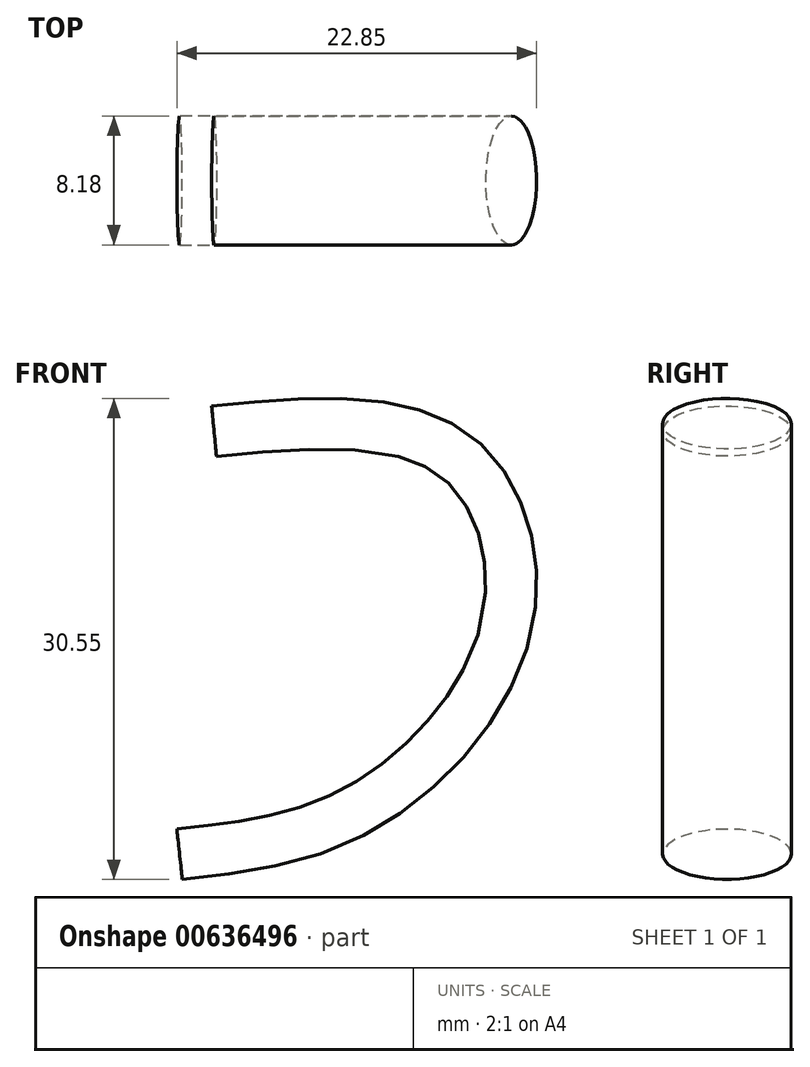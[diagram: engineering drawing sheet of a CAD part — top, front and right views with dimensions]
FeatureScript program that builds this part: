
annotation { "Feature Type Name" : "Feature", "Feature Type Description" : "" }
export const myFeature = defineFeature(function(context is Context, id is Id, definition is map)
    precondition{}
    {
        {
            var Q0;
            Q0=qCreatedBy(makeId("Front.planeOp"),FACE);
            var sketch = newSketch(context, id + "F0", { "sketchPlane" : qUnion([Q0])});
            skLineSegment(sketch, "E0", {"start": v(0, 0) * mm, "end": v(0, 38.86) * mm});
            skSolve(sketch);
        }
        {
            var Q0;
            Q0=qCreatedBy(makeId("Front.planeOp"),FACE);
            var sketch = newSketch(context, id + "F1", { "sketchPlane" : qUnion([Q0])});
            skLineSegment(sketch, "E1", {"start": v(0, 0) * mm, "end": v(11.7, 0) * mm});
            skFitSpline(sketch, "E2", {"points": [v(11.7, 0) * mm, v(19.81, 2.95) * mm, v(26.79, 48.23) * mm], "startDerivative": vector(29.36, 1.38) * mm, "endDerivative": vector(4.15, 84.2) * mm});
            skFitSpline(sketch, "E3", {"points": [v(24.42, 17.48) * mm, v(36.04, 20.46) * mm, v(45.24, 32.13) * mm, v(41.74, 43.02) * mm, v(26.6, 44.43) * mm], "startDerivative": vector(49.86, 5.34) * mm, "endDerivative": vector(-65.27, -6.16) * mm});
            skSolve(sketch);
        }
        {
            var Q0;
            Q0=sQuery(id+"F1.wireOp",EDGE,"E2");
            var Q1;
            Q1=sQuery(id+"F1.wireOp",EDGE,"E1");
            var Q2;
            Q2=sQuery(id+"F0.wireOp",EDGE,"E0");
            revolve(context, id + "F2", {"bodyType" : ToolBodyType.SURFACE, "surfaceEntities" : qUnion([Q0, Q1]), "axis" : qUnion([Q2]), "revolveType" : RevolveType.FULL});
        }
        {
            var Q0;
            Q0=sQuery(id+"F1.wireOp",VERTEX,"E3.end");
            var Q1;
            Q1=sQuery(id+"F1.wireOp",EDGE,"E3");
            cPlane(context, id + "F3", {"entities" : qUnion([Q0, Q1]), "cplaneType" : CPlaneType.CURVE_POINT, "offset" : 25.4 * mm, "width" : 152.4 * mm, "height" : 152.4 * mm});
        }
        {
            var Q0;
            Q0=qCreatedBy(id+"F3.planeOp",FACE);
            var sketch = newSketch(context, id + "F4", { "sketchPlane" : qUnion([Q0])});
            skEllipse(sketch, "E4", {"center": v(0, 41.7) * mm, "majorRadius": 4.09 * mm, "minorRadius": 1.6 * mm, "majorAxis": v(-1, 0)});
            skSolve(sketch);
        }
        {
            var Q0;
            Q0=makeQuery(id+"F4.imprint","IMPRINT",FACE,{"disambiguationData":[TD([[makeQuery(id+"F4.imprint","IMPRINT",EDGE,{"derivedFrom":sQuery(id+"F4.wireOp",EDGE,"E4")}),1.0]])]});
            var Q1;
            Q1=sQuery(id+"F1.wireOp",EDGE,"E3");
            sweep(context, id + "F5", {"profiles" : qUnion([Q0]), "path" : qUnion([Q1])});
        }
    });
